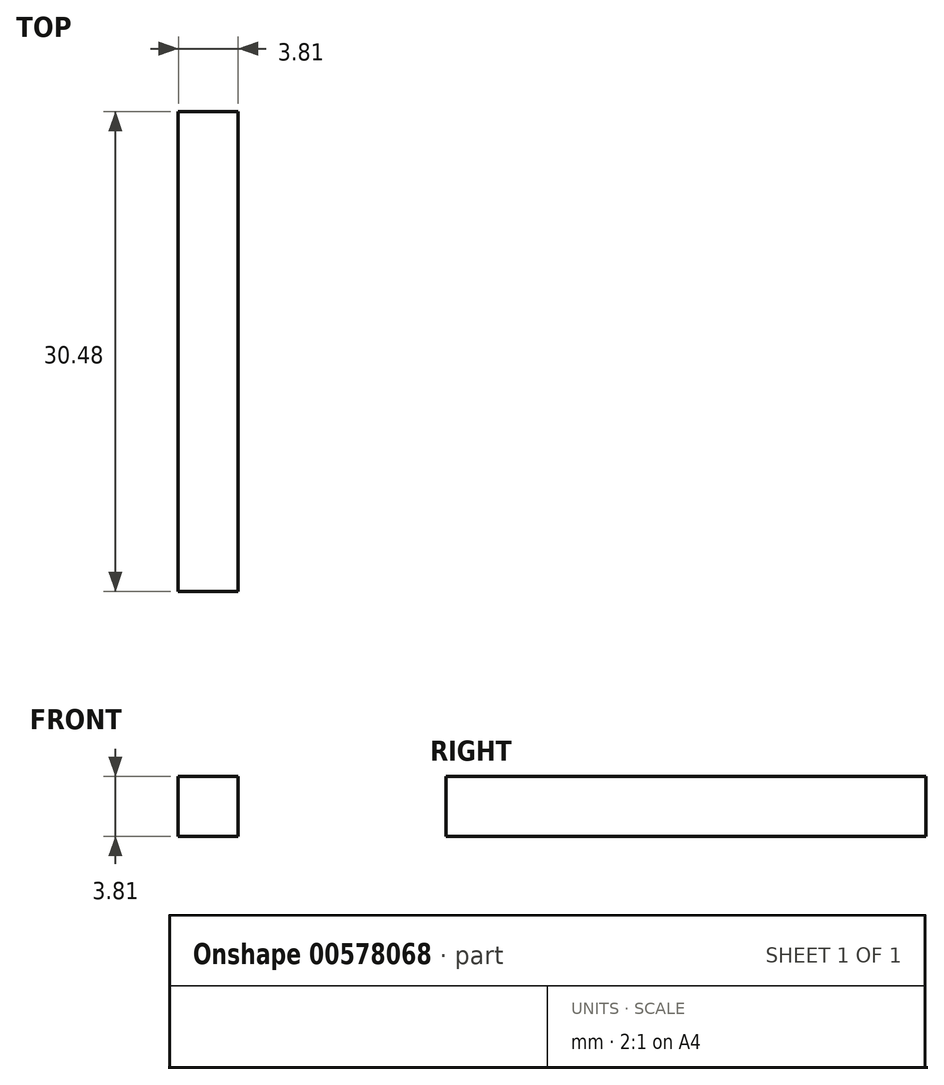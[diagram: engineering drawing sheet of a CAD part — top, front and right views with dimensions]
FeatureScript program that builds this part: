
annotation { "Feature Type Name" : "Feature", "Feature Type Description" : "" }
export const myFeature = defineFeature(function(context is Context, id is Id, definition is map)
    precondition{}
    {
        {
            var Q0;
            Q0=qCreatedBy(makeId("Top.planeOp"),FACE);
            var sketch = newSketch(context, id + "F0", { "sketchPlane" : qUnion([Q0])});
            skLineSegment(sketch, "E0.bottom", {"start": v(20.43, 4.55) * mm, "end": v(24.24, 4.55) * mm});
            skLineSegment(sketch, "E0.top", {"start": v(20.43, -25.93) * mm, "end": v(24.24, -25.93) * mm});
            skLineSegment(sketch, "E0.left", {"start": v(20.43, 4.55) * mm, "end": v(20.43, -25.93) * mm});
            skLineSegment(sketch, "E0.right", {"start": v(24.24, 4.55) * mm, "end": v(24.24, -25.93) * mm});
            skSolve(sketch);
        }
        {
            var Q0;
            Q0 = qSketchRegion(id + "F0", true);
            extrude(context, id + "F1", {"entities" : qUnion([Q0]), "depth" : 3.8 * mm, "offsetDistance" : 25.4 * mm});
        }
    });
